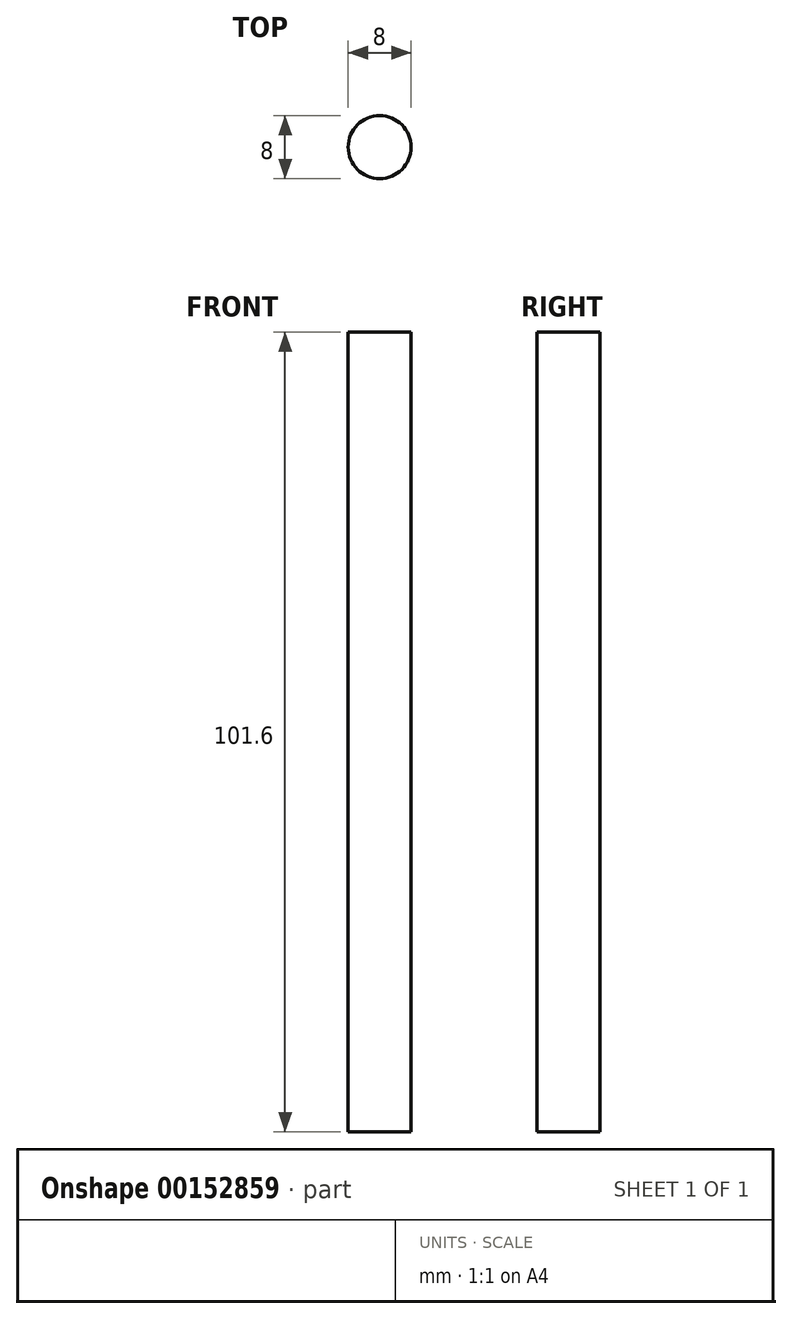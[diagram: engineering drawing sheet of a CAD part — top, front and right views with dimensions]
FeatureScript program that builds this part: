
annotation { "Feature Type Name" : "Feature", "Feature Type Description" : "" }
export const myFeature = defineFeature(function(context is Context, id is Id, definition is map)
    precondition{}
    {
        {
            var Q0;
            Q0=qCreatedBy(makeId("Top.planeOp"),FACE);
            var sketch = newSketch(context, id + "F0", { "sketchPlane" : qUnion([Q0])});
            skCircle(sketch, "E0", {"center": v(0, 0) * mm, "radius": 4 * mm});
            skSolve(sketch);
        }
        {
            var Q0;
            Q0 = qSketchRegion(id + "F0", true);
            extrude(context, id + "F1", {"entities" : qUnion([Q0]), "depth" : 101.6 * mm});
        }
    });
